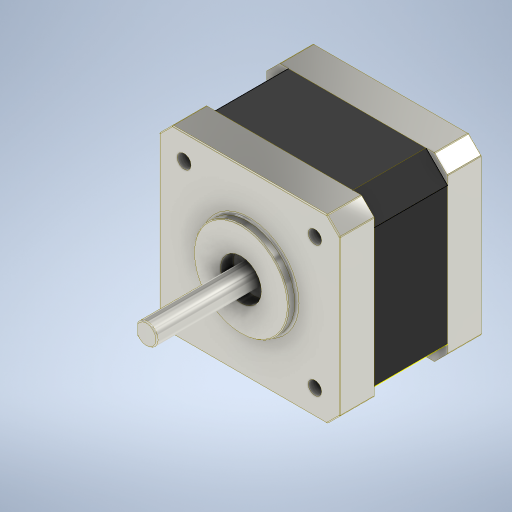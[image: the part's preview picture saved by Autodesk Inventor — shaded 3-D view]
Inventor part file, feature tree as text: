
AUTODESK INVENTOR PART (.ipt)
format: ipt  version: 2024 (Build 280153000, 153)  size: 760,320 bytes
history: native  units: mm
features: extrude x19, chamfer x12, fillet x7, sketch x6, thread x4
ambient origin geometry x8: Origin, YZ Plane, XZ Plane, XY Plane, X Axis, Y Axis, Z Axis, Center Point
bodies: Solid1 (feature_tree)
feature tree (48):
  extrude  "Extrusion1"  Depth=42.0mm
  chamfer  "Chamfer6"  Distance=33.0mm
  chamfer  "Chamfer7"  Distance=3.0mm Angle=45.0deg
  chamfer  "Chamfer8"  Distance=3.0mm Angle=45.0deg
  chamfer  "Chamfer9"  Distance=3.0mm Angle=45.0deg
  chamfer  "Chamfer10"  Distance=8.0mm
  chamfer  "Chamfer11"  Distance=3.0mm Angle=45.0deg
  chamfer  "Chamfer12"  Distance=3.0mm Angle=45.0deg
  chamfer  "Chamfer13"  Distance=8.0mm
  chamfer  "Chamfer14"  Distance=5.0mm Angle=45.0deg
  chamfer  "Chamfer15"  Distance=0.011mm
  chamfer  "Chamfer16"  Distance=3.0mm Angle=45.0deg
  chamfer  "Chamfer17"  Distance=3.0mm Angle=45.0deg
  extrude  "Extrusion3"  Depth=3.0mm TaperAngle=45.0deg
  extrude  "Extrusion4"  Depth=0.01mm TaperAngle=0.0deg
  extrude  "Extrusion5"  Depth=0.01mm TaperAngle=0.0deg
  extrude  "Extrusion6"  Depth=0.01mm TaperAngle=0.0deg
  extrude  "Extrusion7"  Depth=0.01mm TaperAngle=0.0deg
  extrude  "Extrusion8"  Depth=0.05mm
  extrude  "Extrusion9"  Depth=2.0mm TaperAngle=0.0deg
  extrude  "Extrusion10"  Depth=9.5mm
  extrude  "Extrusion11"  Depth=3.0mm TaperAngle=0.0deg
  fillet  "Fillet1"  Radius=5.0mm
  extrude  "Extrusion12"  Depth=25.0mm TaperAngle=0.0deg
  thread  "Thread1"  [1 undecoded]
  thread  "Thread2"  [1 undecoded]
  thread  "Thread3"  [1 undecoded]
  thread  "Thread4"  [1 undecoded]
  extrude  "Extrusion13"  Depth=5.8mm
  extrude  "Extrusion14"  Depth=5.8mm
  extrude  "Extrusion15"  Depth=3.2mm
  fillet  "Fillet2"  Radius=5.8mm
  fillet  "Fillet3"  Radius=5.8mm
  extrude  "Extrusion16"  Depth=3.1mm
  extrude  "Extrusion17"  Depth=5.8mm
  extrude  "Extrusion18"  Depth=5.8mm
  extrude  "Extrusion19"  Depth=3.1mm
  extrude  "Extrusion20"  Depth=5.8mm
  fillet  "Fillet4"  Radius=5.8mm
  fillet  "Fillet5"  Radius=3.1mm
  fillet  "Fillet6"  Radius=50.0mm
  fillet  "Fillet8"  Radius=4.0mm
  sketch  "Sketch10"  dims[d0=42.0mm d1=42.0mm d2=33.0mm d3=0.0mm]
  sketch  "Sketch23"  dims[d32=5.0mm d33=2.0mm d34=45.0deg d35=8.0mm d36=17.0mm d37=8.0mm d38=3.0mm d39=2.0mm d40=45.0deg d41=3.0mm d42=2.0mm d43=45.0deg d44=3.0mm d45=2.0mm d46=45.0deg d47=0.0mm d48=8.0mm d49=25.0mm]
  sketch  "Sketch27"  dims[d50=5.0mm d51=2.0mm d52=45.0deg d53=0.002mm d54=16.998mm d55=8.0mm d56=3.0mm d57=2.0mm d58=45.0deg d59=3.0mm d60=2.0mm d61=45.0deg d62=0.0mm d63=8.0mm d64=25.0mm d65=5.0mm d66=2.0mm d67=45.0deg d68=0.011mm d69=16.989mm d70=8.0mm d71=3.0mm d72=2.0mm d73=45.0deg d74=3.0mm d75=2.0mm d76=45.0deg]
  sketch  "Sketch32"  dims[d77=0.0mm d78=8.0mm d79=25.0mm]
  sketch  "Sketch35"  dims[d80=5.0mm d81=2.0mm d82=45.0deg d83=0.015mm d84=16.985mm d85=8.0mm d86=3.0mm d87=2.0mm d88=45.0deg]
  sketch  "Sketch36"  dims[d89=17.0mm d90=0.0mm d91=0.01mm d92=0.0mm d93=0.01mm d94=0.0mm d95=0.01mm d96=0.0mm d97=0.01mm d98=0.0mm d99=22.0mm d100=2.0mm d101=0.0mm d102=9.5mm d103=3.0mm d104=0.0mm d105=5.0mm d106=25.0mm d107=0.0mm d108=15.0mm d109=4.5mm d110=25.0mm d111=0.0mm d112=0.25mm d113=5.8mm d114=5.8mm d115=3.2mm d116=5.8mm d117=5.8mm d118=3.1mm d119=5.8mm d120=5.8mm d121=3.1mm d122=5.8mm d123=5.8mm d124=3.1mm d125=50.0mm d126=0.0mm d127=4.0mm d128=0.0mm d129=4.0mm d130=0.0mm d131=4.0mm d132=0.0mm d133=4.0mm d134=0.0mm d135=7.0mm d136=4.0mm d137=0.0mm d138=5.8mm d139=5.8mm d140=5.8mm d141=5.8mm d142=2.5mm d143=0.0mm d144=16.0mm d145=8.0mm d146=2.0mm d147=4.3mm d148=0.0mm d149=0.5mm d150=0.2mm d151=5.5mm d152=15.0mm d153=0.5mm d154=6.0mm d155=0.0mm d156=3.9mm d157=13.0mm d158=1.0mm d159=4.5mm d160=0.0mm d161=7.8mm d162=3.9mm d163=4.5mm d164=0.0mm d165=4.0mm d166=1.0mm d167=1.0mm d168=1.0mm d169=1.0mm d170=0.84mm d171=0.0mm d172=0.5mm d173=0.5mm d174=0.5mm d175=1.6mm d176=0.5mm d177=0.5mm d178=0.5mm d179=0.5mm d180=1.6mm d181=1.6mm d182=1.6mm d184=1.6mm d185=1.0mm d186=1.0mm d187=4.0mm d188=0.0mm d189=0.2mm d190=0.3mm d191=0.3mm d193=0.05mm]
note: 4 required parameter values undecoded (feature->parameter linkage not recoverable at this tier; creation-order binding heuristic only, values carry confidence <= 0.55)
